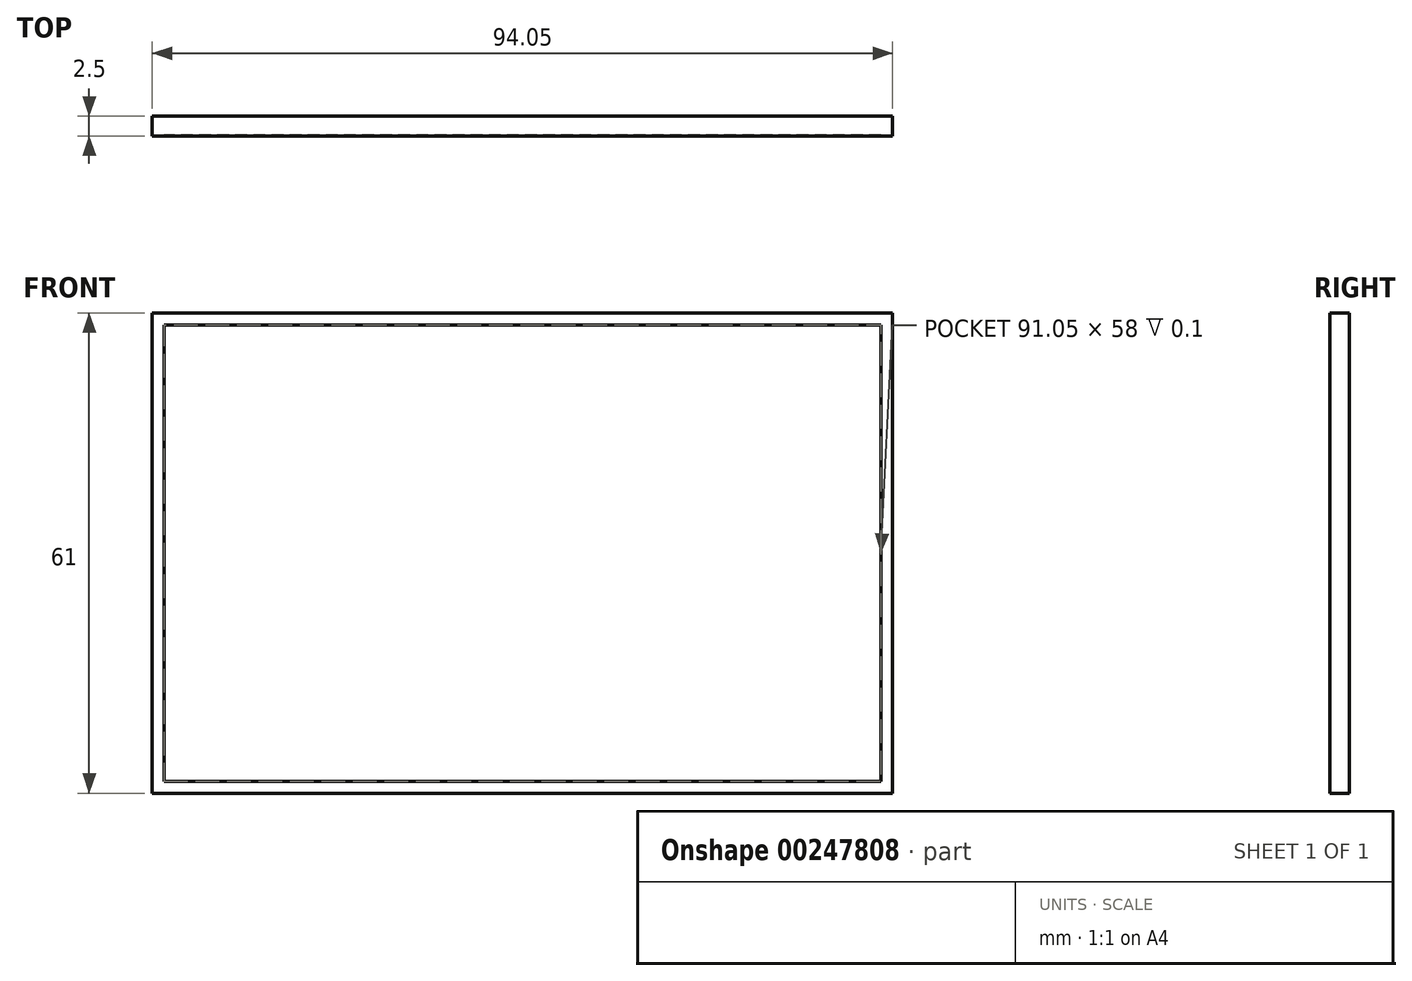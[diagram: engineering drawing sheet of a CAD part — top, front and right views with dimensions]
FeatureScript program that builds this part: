
annotation { "Feature Type Name" : "Feature", "Feature Type Description" : "" }
export const myFeature = defineFeature(function(context is Context, id is Id, definition is map)
    precondition{}
    {
        {
            var Q0;
            Q0=qCreatedBy(makeId("Front.planeOp"),FACE);
            var sketch = newSketch(context, id + "F0", { "sketchPlane" : qUnion([Q0])});
            skLineSegment(sketch, "E0.bottom", {"start": v(0, 0) * mm, "end": v(94.05, 0) * mm});
            skLineSegment(sketch, "E0.top", {"start": v(0, 61) * mm, "end": v(94.05, 61) * mm});
            skLineSegment(sketch, "E0.left", {"start": v(0, 0) * mm, "end": v(0, 61) * mm});
            skLineSegment(sketch, "E0.right", {"start": v(94.05, 0) * mm, "end": v(94.05, 61) * mm});
            skSolve(sketch);
        }
        {
            var Q0;
            Q0 = qSketchRegion(id + "F0", true);
            extrude(context, id + "F1", {"entities" : qUnion([Q0]), "depth" : 2.5 * mm});
        }
        {
            var Q0;
            Q0=makeQuery(id+"F1.opExtrude","CAP_FACE",FACE,{"disambiguationData":[OSD([sQuery(id+"F0.wireOp",EDGE,"E0.bottom"),sQuery(id+"F0.wireOp",EDGE,"E0.top"),sQuery(id+"F0.wireOp",EDGE,"E0.left"),sQuery(id+"F0.wireOp",EDGE,"E0.right")])],"isStart":false});
            var sketch = newSketch(context, id + "F2", { "sketchPlane" : qUnion([Q0])});
            skLineSegment(sketch, "E1.0", {"start": v(92.55, 59.5) * mm, "end": v(1.5, 59.5) * mm});
            skLineSegment(sketch, "E1.1", {"start": v(92.55, 1.5) * mm, "end": v(92.55, 59.5) * mm});
            skLineSegment(sketch, "E1.2", {"start": v(1.5, 1.5) * mm, "end": v(92.55, 1.5) * mm});
            skLineSegment(sketch, "E1.3", {"start": v(1.5, 59.5) * mm, "end": v(1.5, 1.5) * mm});
            skSolve(sketch);
        }
        {
            var Q0;
            Q0 = qSketchRegion(id + "F2", true);
            extrude(context, id + "F3", {"entities" : qUnion([Q0]), "operationType" : NewBodyOperationType.REMOVE, "oppositeDirection" : true, "depth" : .1 * mm});
        }
    });
